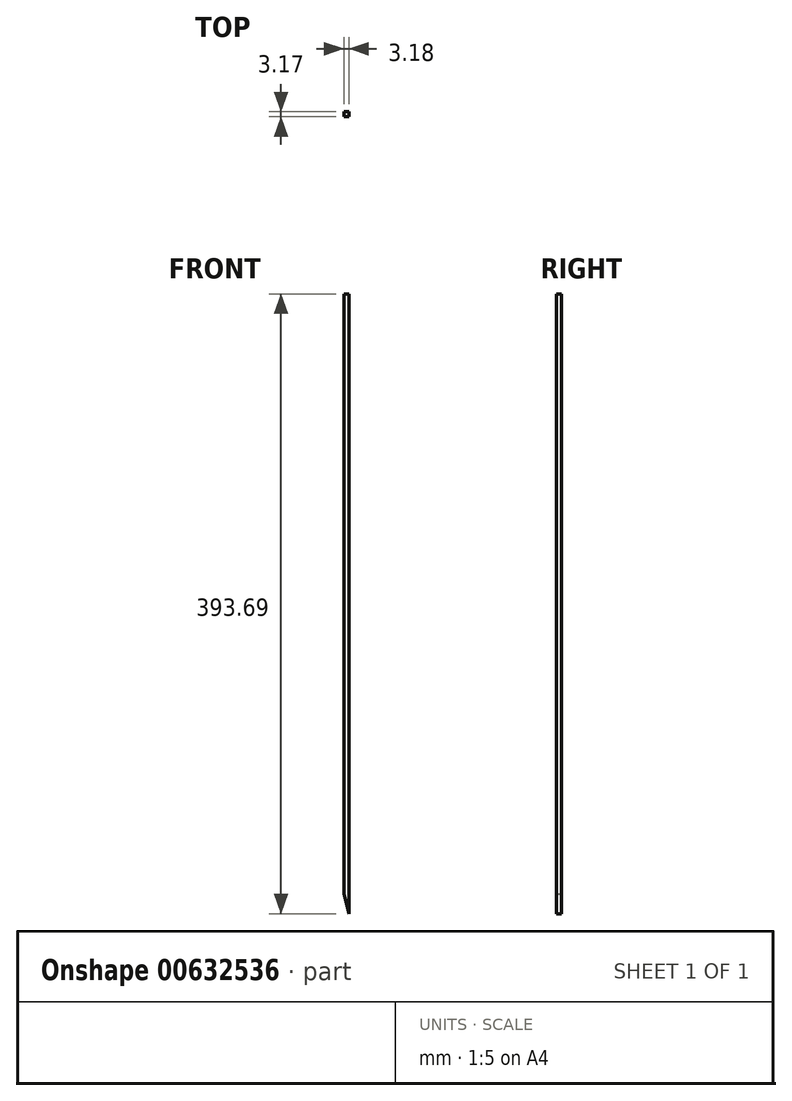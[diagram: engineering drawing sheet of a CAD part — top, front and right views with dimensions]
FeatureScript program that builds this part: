
annotation { "Feature Type Name" : "Feature", "Feature Type Description" : "" }
export const myFeature = defineFeature(function(context is Context, id is Id, definition is map)
    precondition{}
    {
        {
            var Q0;
            Q0=qCreatedBy(makeId("Front.planeOp"),FACE);
            var sketch = newSketch(context, id + "F0", { "sketchPlane" : qUnion([Q0])});
            skLineSegment(sketch, "E0", {"start": v(-12.03, -18.6) * mm, "end": v(-12.03, 375.1) * mm});
            skLineSegment(sketch, "E1", {"start": v(-12.03, 375.1) * mm, "end": v(-15.2, 375.1) * mm});
            skLineSegment(sketch, "E2", {"start": v(-15.2, 375.1) * mm, "end": v(-15.2, -5.9) * mm});
            skLineSegment(sketch, "E3", {"start": v(-15.2, -5.9) * mm, "end": v(-12.03, -18.6) * mm});
            skSolve(sketch);
        }
        {
            var Q0;
            Q0=makeQuery(id+"F0.imprint","IMPRINT",FACE,{"disambiguationData":[TD([[makeQuery(id+"F0.imprint","IMPRINT",EDGE,{"derivedFrom":sQuery(id+"F0.wireOp",EDGE,"E0")}),1.0]])]});
            extrude(context, id + "F1", {"entities" : qUnion([Q0]), "depth" : 3.17 * mm, "offsetDistance" : 25.4 * mm});
        }
    });
